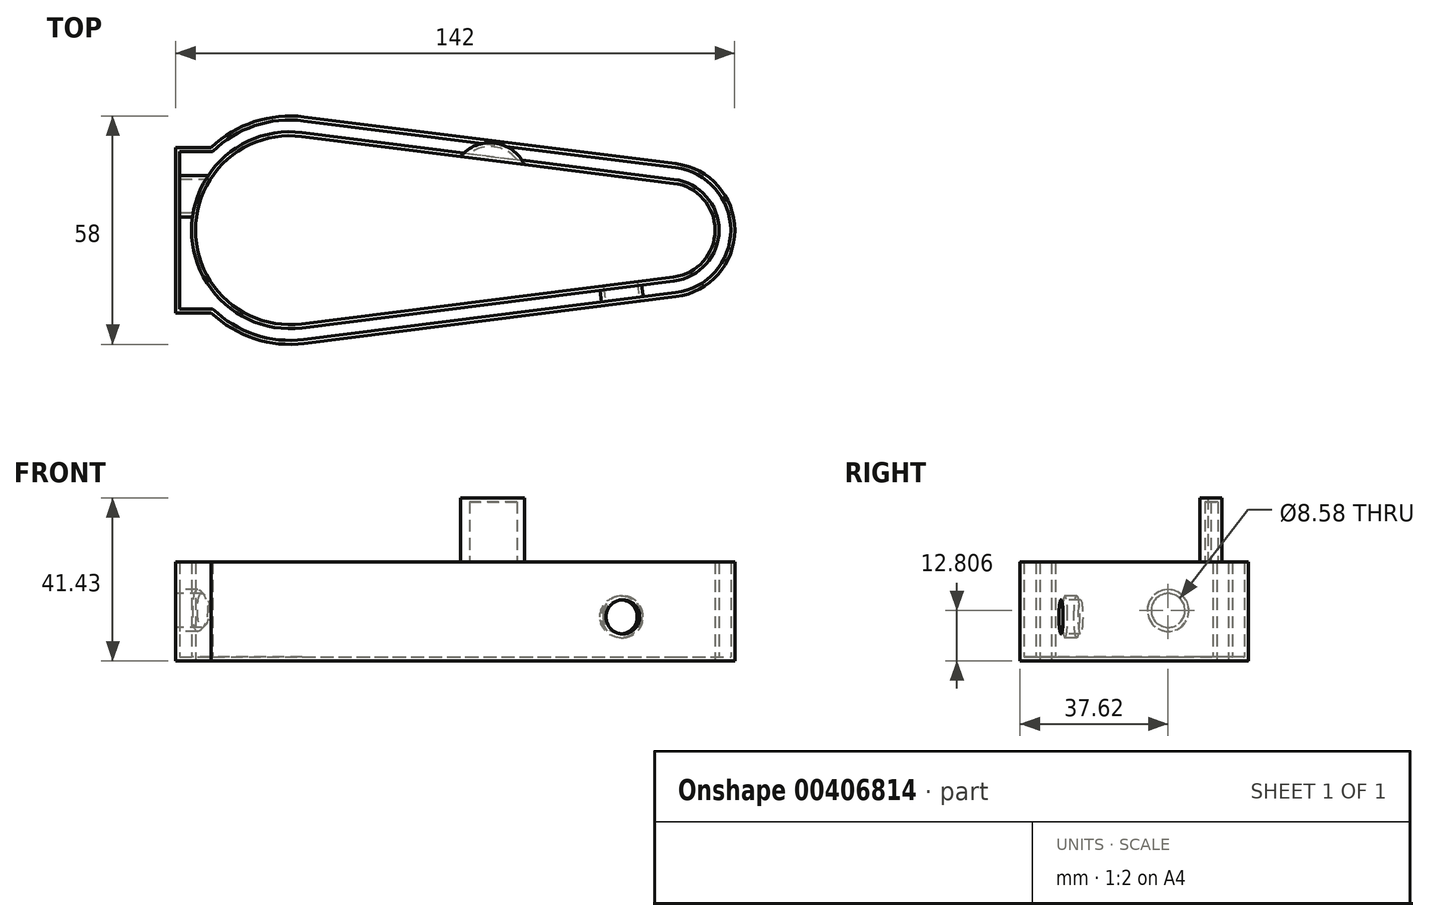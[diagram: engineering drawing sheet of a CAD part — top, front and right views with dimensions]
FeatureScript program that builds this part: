
annotation { "Feature Type Name" : "Feature", "Feature Type Description" : "" }
export const myFeature = defineFeature(function(context is Context, id is Id, definition is map)
    precondition{}
    {
        {
            var Q0;
            Q0=qCreatedBy(makeId("Top.planeOp"),FACE);
            var sketch = newSketch(context, id + "F0", { "sketchPlane" : qUnion([Q0])});
            skArc(sketch, "E0", {"start": v(-40.6, 27.78) * mm, "mid": v(-72.1, 0) * mm, "end": v(-40.6, -27.78) * mm});
            skArc(sketch, "E1", {"start": v(53.9, -15.87) * mm, "mid": v(67.9, 0) * mm, "end": v(53.9, 15.87) * mm});
            skLineSegment(sketch, "E2", {"start": v(-40.6, 27.78) * mm, "end": v(53.9, 15.87) * mm});
            skLineSegment(sketch, "E3", {"start": v(-40.6, -27.78) * mm, "end": v(53.9, -15.87) * mm});
            skLineSegment(sketch, "E4", {"start": v(-72.1, 0) * mm, "end": v(-72.1, 20) * mm});
            skLineSegment(sketch, "E5", {"start": v(-72.1, 0) * mm, "end": v(-72.1, -20) * mm});
            skLineSegment(sketch, "E6", {"start": v(-72.1, 20) * mm, "end": v(-63.7, 20) * mm});
            skLineSegment(sketch, "E7", {"start": v(-72.1, -20) * mm, "end": v(-63.7, -20) * mm});
            skArc(sketch, "E8", {"start": v(-40.97, 24.8) * mm, "mid": v(-69.1, 0) * mm, "end": v(-40.97, -24.8) * mm});
            skArc(sketch, "E9", {"start": v(53.53, -12.9) * mm, "mid": v(64.9, 0) * mm, "end": v(53.53, 12.9) * mm});
            skLineSegment(sketch, "E10", {"start": v(-40.97, 24.8) * mm, "end": v(53.53, 12.9) * mm});
            skLineSegment(sketch, "E11", {"start": v(-40.97, -24.8) * mm, "end": v(53.53, -12.9) * mm});
            skLineSegment(sketch, "E12", {"start": v(-40.97, 24.8) * mm, "end": v(-69.1, 0) * mm});
            skLineSegment(sketch, "E13", {"start": v(-69.1, 0) * mm, "end": v(-40.97, -24.8) * mm});
            skSolve(sketch);
        }
        {
            var Q0;
            Q0 = qSketchRegion(id + "F0", true);
            var Q1;
            Q1 = qConstructionFilter(qBodyType(qCreatedBy(id + "F0" ,EDGE), BodyType.WIRE), ConstructionObject.NO);
            extrude(context, id + "F1", {"entities" : qUnion([Q0]), "surfaceEntities" : qUnion([Q1]), "depth" : 24.13 * mm});
        }
        {
            var Q0;
            Q0=makeQuery(id+"F1.opExtrude","CAP_FACE",FACE,{"disambiguationData":[OSD([sQuery(id+"F0.wireOp",EDGE,"E0"),sQuery(id+"F0.wireOp",EDGE,"E1"),sQuery(id+"F0.wireOp",EDGE,"E2"),sQuery(id+"F0.wireOp",EDGE,"E3"),sQuery(id+"F0.wireOp",EDGE,"E4"),sQuery(id+"F0.wireOp",EDGE,"E5"),sQuery(id+"F0.wireOp",EDGE,"E6"),sQuery(id+"F0.wireOp",EDGE,"E7"),sQuery(id+"F0.wireOp",EDGE,"E8"),sQuery(id+"F0.wireOp",EDGE,"E9"),sQuery(id+"F0.wireOp",EDGE,"E10"),sQuery(id+"F0.wireOp",EDGE,"E11")])],"isStart":false});
            var sketch = newSketch(context, id + "F2", { "sketchPlane" : qUnion([Q0])});
            skCircle(sketch, "E14", {"center": v(6.73, 12.53) * mm, "radius": 8.7 * mm});
            skCircle(sketch, "E15", {"center": v(6.73, 12.53) * mm, "radius": 5.71 * mm});
            skCircle(sketch, "E16", {"center": v(-43.75, 12.07) * mm, "radius": 7.32 * mm});
            skSolve(sketch);
        }
        {
            var Q0;
            Q0=makeQuery(id+"F2.imprint","IMPRINT",FACE,{"disambiguationData":[TD([[makeQuery(id+"F2.imprint","IMPRINT",EDGE,{"derivedFrom":sQuery(id+"F2.wireOp",EDGE,"E14")}),1.0]])]});
            extrude(context, id + "F3", {"entities" : qUnion([Q0]), "operationType" : NewBodyOperationType.ADD, "depth" : 15.3 * mm});
        }
        {
            var Q0;
            {var subQ0=sQuery(id+"F0.wireOp",EDGE,"E1");var subQ1=sQuery(id+"F0.wireOp",EDGE,"E3");Q0=makeQuery(id+"F3.boolean.opBoolean","SPLIT",FACE,{"disambiguationData":[TD([makeQuery(id+"F1.opExtrude","SWEPT_FACE",FACE,{"disambiguationData":[OSD([subQ0])]})])],"derivedFrom":makeQuery(id+"F1.opExtrude","SWEPT_FACE",FACE,{"disambiguationData":[OSD([subQ1])]})});}
            var sketch = newSketch(context, id + "F4", { "sketchPlane" : qUnion([Q0])});
            skCircle(sketch, "E17", {"center": v(37.83, 10.19) * mm, "radius": 5.33 * mm});
            skSolve(sketch);
        }
        {
            var Q0;
            Q0=makeQuery(id+"F4.imprint","IMPRINT",FACE,{"disambiguationData":[TD([[makeQuery(id+"F4.imprint","IMPRINT",EDGE,{"derivedFrom":sQuery(id+"F4.wireOp",EDGE,"E17")}),1.0]])]});
            var Q1;
            Q1=sQuery(id+"F4.wireOp",EDGE,"E17");
            extrude(context, id + "F5", {"entities" : qUnion([Q0]), "operationType" : NewBodyOperationType.REMOVE, "surfaceEntities" : qUnion([Q1]), "oppositeDirection" : true, "depth" : 13.3 * mm});
        }
        {
            var Q0;
            Q0=makeQuery(id+"F1.opExtrude","SWEPT_FACE",FACE,{"disambiguationData":[OSD([sQuery(id+"F0.wireOp",EDGE,"E4"),sQuery(id+"F0.wireOp",EDGE,"E5")])]});
            var sketch = newSketch(context, id + "F6", { "sketchPlane" : qUnion([Q0])});
            skCircle(sketch, "E18", {"center": v(-8.62, 11.8) * mm, "radius": 5.3 * mm});
            skSolve(sketch);
        }
        {
            var Q0;
            Q0=makeQuery(id+"F6.imprint","IMPRINT",FACE,{"disambiguationData":[TD([[makeQuery(id+"F6.imprint","IMPRINT",EDGE,{"derivedFrom":sQuery(id+"F6.wireOp",EDGE,"E18")}),1.0]])]});
            var Q1;
            Q1=sQuery(id+"F6.wireOp",EDGE,"E18");
            extrude(context, id + "F7", {"entities" : qUnion([Q0]), "operationType" : NewBodyOperationType.REMOVE, "surfaceEntities" : qUnion([Q1]), "oppositeDirection" : true, "depth" : 27.2 * mm});
        }
        {
            var Q0;
            Q0=makeQuery(id+"F1.opExtrude","CAP_FACE",FACE,{"disambiguationData":[OSD([sQuery(id+"F0.wireOp",EDGE,"E0"),sQuery(id+"F0.wireOp",EDGE,"E1"),sQuery(id+"F0.wireOp",EDGE,"E2"),sQuery(id+"F0.wireOp",EDGE,"E3"),sQuery(id+"F0.wireOp",EDGE,"E4"),sQuery(id+"F0.wireOp",EDGE,"E5"),sQuery(id+"F0.wireOp",EDGE,"E6"),sQuery(id+"F0.wireOp",EDGE,"E7"),sQuery(id+"F0.wireOp",EDGE,"E8"),sQuery(id+"F0.wireOp",EDGE,"E9"),sQuery(id+"F0.wireOp",EDGE,"E10"),sQuery(id+"F0.wireOp",EDGE,"E11")])],"isStart":false});
            shell(context, id + "F8", {"entities" : qUnion([Q0]), "thickness" : 1 * mm, "oppositeDirection" : true});
        }
    });
